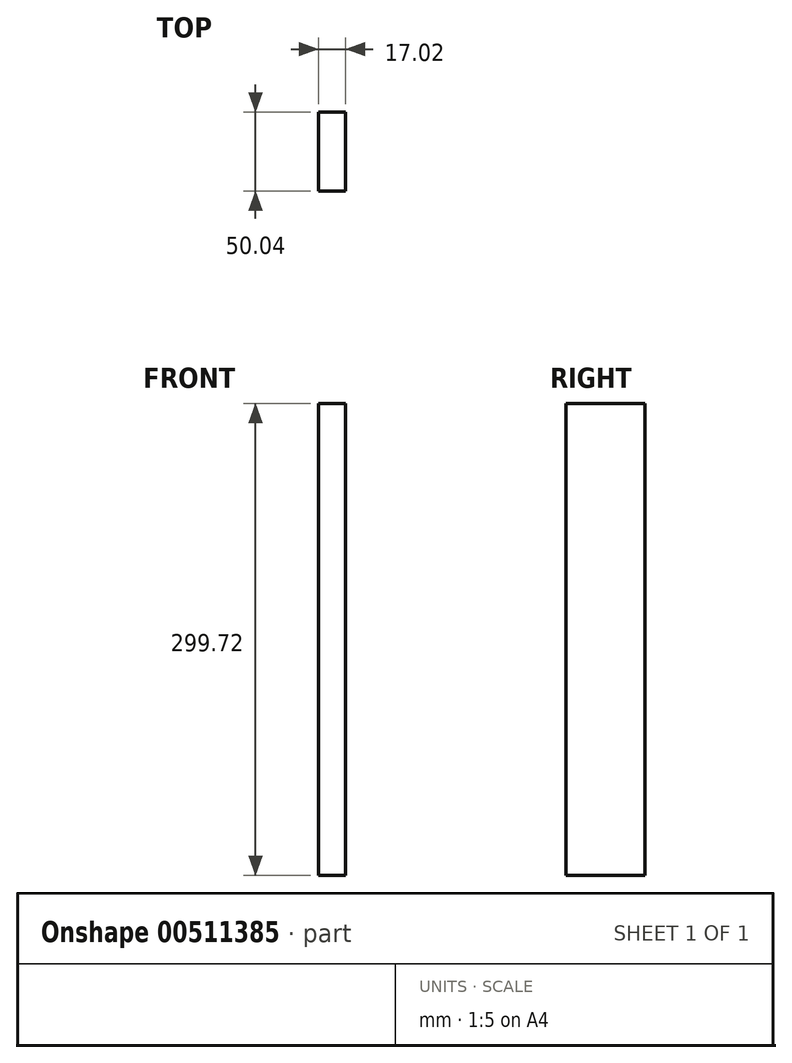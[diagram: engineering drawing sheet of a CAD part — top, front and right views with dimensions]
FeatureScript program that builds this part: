
annotation { "Feature Type Name" : "Feature", "Feature Type Description" : "" }
export const myFeature = defineFeature(function(context is Context, id is Id, definition is map)
    precondition{}
    {
        {
            var Q0;
            Q0=qCreatedBy(makeId("Right.planeOp"),FACE);
            var sketch = newSketch(context, id + "F0", { "sketchPlane" : qUnion([Q0])});
            skLineSegment(sketch, "E0.bottom", {"start": v(-25.02, 149.86) * mm, "end": v(25.02, 149.86) * mm});
            skLineSegment(sketch, "E0.top", {"start": v(-25.02, -149.86) * mm, "end": v(25.02, -149.86) * mm});
            skLineSegment(sketch, "E0.left", {"start": v(-25.02, 149.86) * mm, "end": v(-25.02, -149.86) * mm});
            skLineSegment(sketch, "E0.right", {"start": v(25.02, 149.86) * mm, "end": v(25.02, -149.86) * mm});
            skPoint(sketch, "E0.middle", {"position": v(0, 0) * mm});
            skSolve(sketch);
        }
        {
            var Q0;
            Q0=makeQuery(id+"F0.imprint","IMPRINT",FACE,{"disambiguationData":[TD([[makeQuery(id+"F0.imprint","IMPRINT",EDGE,{"derivedFrom":sQuery(id+"F0.wireOp",EDGE,"E0.bottom")}),-1.0]])]});
            extrude(context, id + "F1", {"entities" : qUnion([Q0]), "endBound" : BoundingType.SYMMETRIC, "depth" : 17.02 * mm, "offsetDistance" : 25.4 * mm});
        }
        {
            var Q0;
            Q0=makeQuery(id+"F1.opExtrude","CAP_FACE",FACE,{"disambiguationData":[OSD([sQuery(id+"F0.wireOp",EDGE,"E0.bottom"),sQuery(id+"F0.wireOp",EDGE,"E0.top"),sQuery(id+"F0.wireOp",EDGE,"E0.left"),sQuery(id+"F0.wireOp",EDGE,"E0.right")])],"isStart":false});
            var sketch = newSketch(context, id + "F2", { "sketchPlane" : qUnion([Q0])});
            skLineSegment(sketch, "E1.bottom", {"start": v(-25.02, 149.86) * mm, "end": v(25.02, 149.86) * mm});
            skLineSegment(sketch, "E1.top", {"start": v(-25.02, 132.84) * mm, "end": v(25.02, 132.84) * mm});
            skLineSegment(sketch, "E1.left", {"start": v(-25.02, 149.86) * mm, "end": v(-25.02, 132.84) * mm});
            skLineSegment(sketch, "E1.right", {"start": v(25.02, 149.86) * mm, "end": v(25.02, 132.84) * mm});
            skSolve(sketch);
        }
        {
            var Q0;
            Q0=makeQuery(id+"F1.opExtrude","CAP_FACE",FACE,{"disambiguationData":[OSD([sQuery(id+"F0.wireOp",EDGE,"E0.bottom"),sQuery(id+"F0.wireOp",EDGE,"E0.top"),sQuery(id+"F0.wireOp",EDGE,"E0.left"),sQuery(id+"F0.wireOp",EDGE,"E0.right")])],"isStart":true});
            var sketch = newSketch(context, id + "F3", { "sketchPlane" : qUnion([Q0])});
            skLineSegment(sketch, "E2.bottom", {"start": v(-25.02, 149.86) * mm, "end": v(25.02, 149.86) * mm});
            skLineSegment(sketch, "E2.top", {"start": v(-25.02, 132.84) * mm, "end": v(25.02, 132.84) * mm});
            skLineSegment(sketch, "E2.left", {"start": v(-25.02, 149.86) * mm, "end": v(-25.02, 132.84) * mm});
            skLineSegment(sketch, "E2.right", {"start": v(25.02, 149.86) * mm, "end": v(25.02, 132.84) * mm});
            skSolve(sketch);
        }
    });
